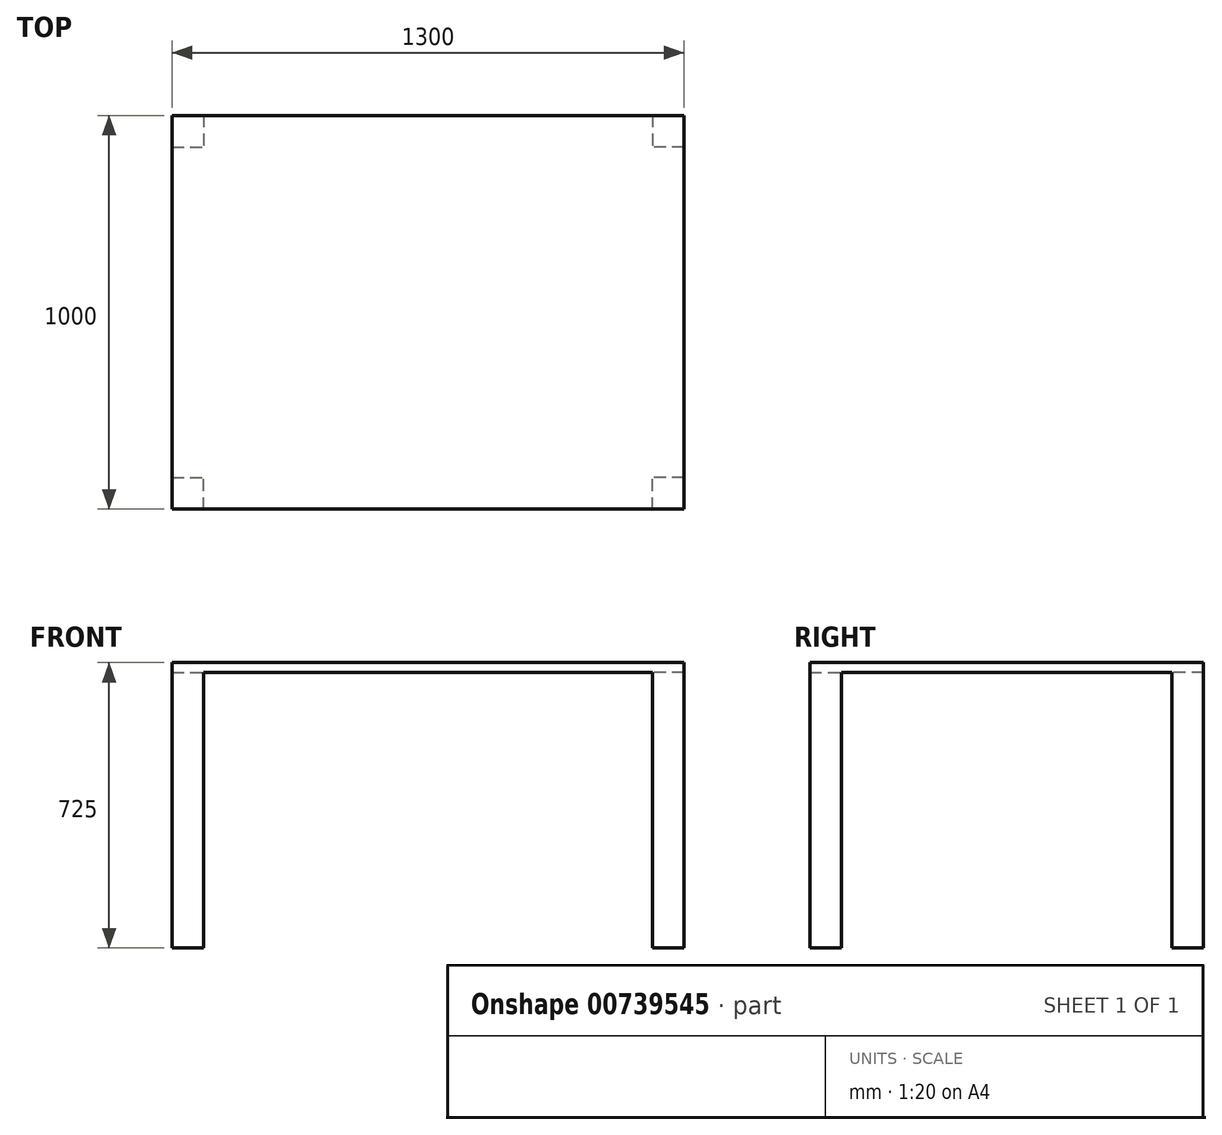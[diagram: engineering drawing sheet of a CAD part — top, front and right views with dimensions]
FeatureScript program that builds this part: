
annotation { "Feature Type Name" : "Feature", "Feature Type Description" : "" }
export const myFeature = defineFeature(function(context is Context, id is Id, definition is map)
    precondition{}
    {
        {
            var Q0;
            Q0=qCreatedBy(makeId("Top.planeOp"),FACE);
            var sketch = newSketch(context, id + "F0", { "sketchPlane" : qUnion([Q0])});
            skLineSegment(sketch, "E0.bottom", {"start": v(650, -500) * mm, "end": v(-650, -500) * mm});
            skLineSegment(sketch, "E0.top", {"start": v(650, 500) * mm, "end": v(-650, 500) * mm});
            skLineSegment(sketch, "E0.left", {"start": v(650, -500) * mm, "end": v(650, 500) * mm});
            skLineSegment(sketch, "E0.right", {"start": v(-650, -500) * mm, "end": v(-650, 500) * mm});
            skPoint(sketch, "E0.middle", {"position": v(0, 0) * mm});
            skSolve(sketch);
        }
        {
            var Q0;
            Q0 = qSketchRegion(id + "F0", true);
            extrude(context, id + "F1", {"entities" : qUnion([Q0]), "depth" : 25 * mm, "offsetDistance" : 25 * mm});
        }
        {
            var Q0;
            Q0=makeQuery(id+"F1.opExtrude","CAP_FACE",FACE,{"disambiguationData":[OSD([sQuery(id+"F0.wireOp",EDGE,"E0.bottom"),sQuery(id+"F0.wireOp",EDGE,"E0.top"),sQuery(id+"F0.wireOp",EDGE,"E0.left"),sQuery(id+"F0.wireOp",EDGE,"E0.right")])],"isStart":true});
            var sketch = newSketch(context, id + "F2", { "sketchPlane" : qUnion([Q0])});
            skLineSegment(sketch, "E1.bottom", {"start": v(-650, 500) * mm, "end": v(-570, 500) * mm});
            skLineSegment(sketch, "E1.top", {"start": v(-650, 420) * mm, "end": v(-570, 420) * mm});
            skLineSegment(sketch, "E1.left", {"start": v(-650, 500) * mm, "end": v(-650, 420) * mm});
            skLineSegment(sketch, "E1.right", {"start": v(-570, 500) * mm, "end": v(-570, 420) * mm});
            skLineSegment(sketch, "E2.MirrorCS", {"start": v(570, 500) * mm, "end": v(570, 420) * mm});
            skLineSegment(sketch, "E3.MirrorCS", {"start": v(650, 500) * mm, "end": v(650, 420) * mm});
            skLineSegment(sketch, "E4.MirrorCS", {"start": v(650, 420) * mm, "end": v(570, 420) * mm});
            skLineSegment(sketch, "E5.MirrorCS", {"start": v(650, 500) * mm, "end": v(570, 500) * mm});
            skLineSegment(sketch, "E6.MirrorCS", {"start": v(650, -420) * mm, "end": v(570, -420) * mm});
            skLineSegment(sketch, "E7.MirrorCS", {"start": v(650, -500) * mm, "end": v(650, -420) * mm});
            skLineSegment(sketch, "E8.MirrorCS", {"start": v(570, -500) * mm, "end": v(570, -420) * mm});
            skLineSegment(sketch, "E9.MirrorCS", {"start": v(-570, -500) * mm, "end": v(-570, -420) * mm});
            skLineSegment(sketch, "E10.MirrorCS", {"start": v(-650, -500) * mm, "end": v(-650, -420) * mm});
            skLineSegment(sketch, "E11.MirrorCS", {"start": v(-650, -420) * mm, "end": v(-570, -420) * mm});
            skLineSegment(sketch, "E12.MirrorCS", {"start": v(-650, -500) * mm, "end": v(-570, -500) * mm});
            skLineSegment(sketch, "E13.MirrorCS", {"start": v(650, -500) * mm, "end": v(570, -500) * mm});
            skSolve(sketch);
        }
        {
            var Q0;
            Q0 = qSketchRegion(id + "F2", true);
            extrude(context, id + "F3", {"entities" : qUnion([Q0]), "operationType" : NewBodyOperationType.ADD, "depth" : 700 * mm, "offsetDistance" : 25 * mm});
        }
    });
